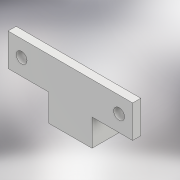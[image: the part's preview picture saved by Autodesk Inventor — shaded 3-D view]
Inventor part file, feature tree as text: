
AUTODESK INVENTOR PART (.ipt)
format: ipt  version: 2018.2 (Build 222227000, 227)  size: 134,144 bytes
history: native  units: mm
features: extrude x2, sketch x2, fillet x1
ambient origin geometry x8: Origin, YZ Plane, XZ Plane, XY Plane, X Axis, Y Axis, Z Axis, Center Point
bodies: Solid1 (feature_tree)
feature tree (5):
  extrude  "Extrusion1"  Depth=8.0mm
  extrude  "Extrusion2"  Depth=26.0mm
  fillet  "Fillet1"  Radius=4.0mm
  sketch  "Sketch1"  dims[d0=14.0mm d9=8.0mm]
  sketch  "Sketch2"  dims[d10=10.0mm d11=0.0mm d13=26.0mm d14=4.0mm d15=4.0mm d16=36.0mm d17=6.0mm d18=46.0mm d19=3.0mm d20=0.0mm d21=6.0mm]
